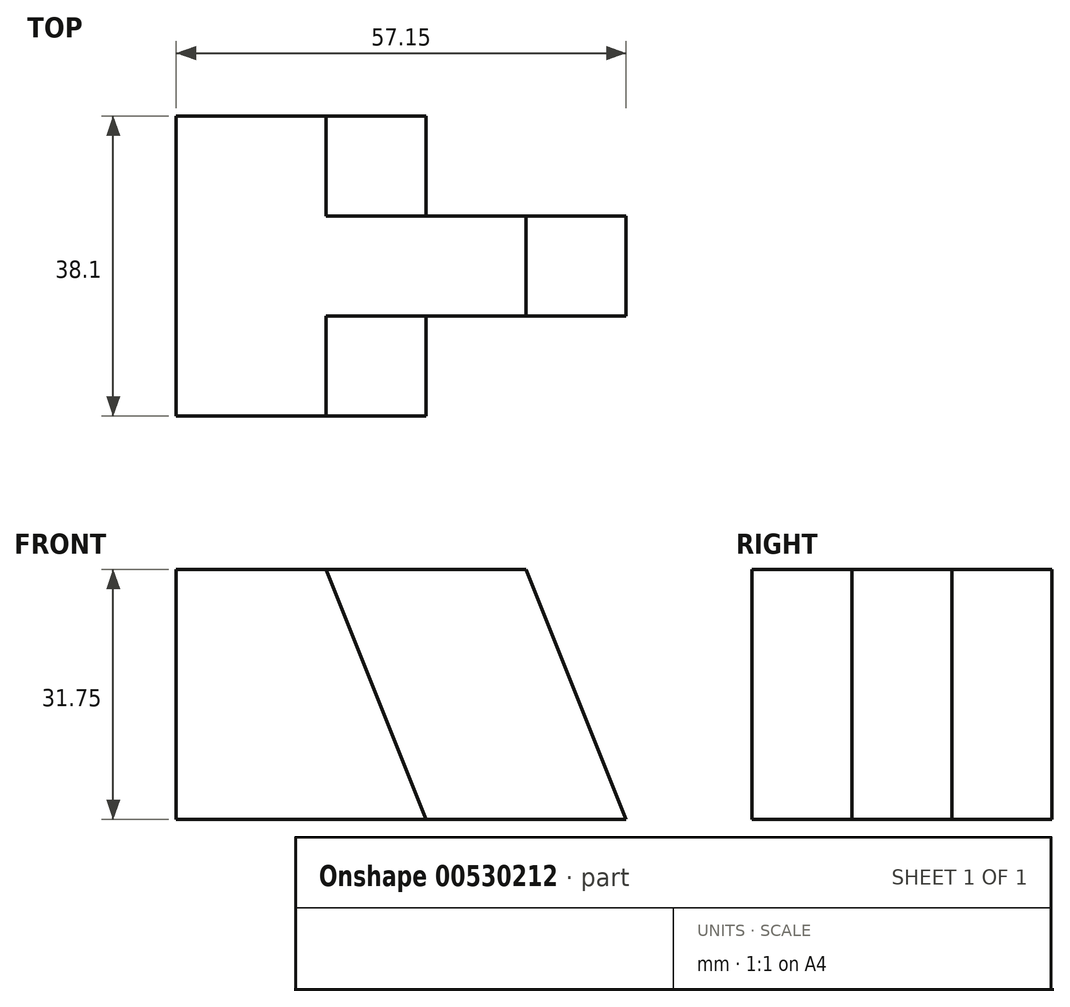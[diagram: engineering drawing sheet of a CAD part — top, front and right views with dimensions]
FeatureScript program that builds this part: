
annotation { "Feature Type Name" : "Feature", "Feature Type Description" : "" }
export const myFeature = defineFeature(function(context is Context, id is Id, definition is map)
    precondition{}
    {
        {
            var Q0;
            Q0=qCreatedBy(makeId("Top.planeOp"),FACE);
            var sketch = newSketch(context, id + "F0", { "sketchPlane" : qUnion([Q0])});
            skLineSegment(sketch, "E0", {"start": v(-47.77, 0) * mm, "end": v(-47.77, -38.1) * mm});
            skLineSegment(sketch, "E1", {"start": v(-47.77, -38.1) * mm, "end": v(-28.72, -38.1) * mm});
            skLineSegment(sketch, "E2", {"start": v(-28.72, -38.1) * mm, "end": v(-28.72, 0) * mm});
            skLineSegment(sketch, "E3", {"start": v(-28.72, 0) * mm, "end": v(-47.77, 0) * mm});
            skSolve(sketch);
        }
        {
            var Q0;
            Q0=makeQuery(id+"F0.imprint","IMPRINT",FACE,{"disambiguationData":[TD([[makeQuery(id+"F0.imprint","IMPRINT",EDGE,{"derivedFrom":sQuery(id+"F0.wireOp",EDGE,"E0")}),1.0]])]});
            extrude(context, id + "F1", {"entities" : qUnion([Q0]), "depth" : 31.75 * mm, "offsetDistance" : 25.4 * mm});
        }
        {
            var Q0;
            Q0=makeQuery(id+"F1.opExtrude","SWEPT_FACE",FACE,{"disambiguationData":[OSD([sQuery(id+"F0.wireOp",EDGE,"E2")])]});
            var sketch = newSketch(context, id + "F2", { "sketchPlane" : qUnion([Q0])});
            skLineSegment(sketch, "E4", {"start": v(-38.1, 31.75) * mm, "end": v(-25.4, 31.75) * mm});
            skLineSegment(sketch, "E5", {"start": v(-25.4, 31.75) * mm, "end": v(-25.4, 0) * mm});
            skLineSegment(sketch, "E6", {"start": v(-25.4, 0) * mm, "end": v(-38.1, 0) * mm});
            skLineSegment(sketch, "E7", {"start": v(-38.1, 0) * mm, "end": v(-38.1, 31.75) * mm});
            skSolve(sketch);
        }
        {
            var Q0;
            Q0=makeQuery(id+"F2.imprint","IMPRINT",FACE,{"disambiguationData":[TD([[makeQuery(id+"F2.imprint","IMPRINT",EDGE,{"derivedFrom":sQuery(id+"F2.wireOp",EDGE,"E4")}),-1.0]])]});
            extrude(context, id + "F3", {"entities" : qUnion([Q0]), "operationType" : NewBodyOperationType.ADD, "depth" : 12.7 * mm, "offsetDistance" : 25.4 * mm});
        }
        {
            var Q0;
            Q0=makeQuery(id+"F3.boolean.opBoolean","MERGE",FACE,{"derivedFrom":[makeQuery(id+"F1.opExtrude","SWEPT_FACE",FACE,{"disambiguationData":[OSD([sQuery(id+"F0.wireOp",EDGE,"E1")])]}),makeQuery(id+"F3.opExtrude","SWEPT_FACE",FACE,{"disambiguationData":[OSD([sQuery(id+"F2.wireOp",EDGE,"E7")])]})]});
            var sketch = newSketch(context, id + "F4", { "sketchPlane" : qUnion([Q0])});
            skLineSegment(sketch, "E8", {"start": v(-16.02, 0) * mm, "end": v(-28.72, 31.75) * mm});
            skSolve(sketch);
        }
        {
            var Q0;
            {var subQ0=sQuery(id+"F4.wireOp",EDGE,"E8");Q0=makeQuery(id+"F4.imprint","IMPRINT",FACE,{"disambiguationData":[TD([[makeQuery(id+"F4.imprint","IMPRINT",EDGE,{"derivedFrom":subQ0}),-1.0]])]});}
            extrude(context, id + "F5", {"entities" : qUnion([Q0]), "operationType" : NewBodyOperationType.REMOVE, "oppositeDirection" : true, "depth" : 25.4 * mm, "offsetDistance" : 25.4 * mm});
        }
        {
            var Q0;
            Q0=makeQuery(id+"F1.opExtrude","SWEPT_FACE",FACE,{"disambiguationData":[OSD([sQuery(id+"F0.wireOp",EDGE,"E2")])]});
            var sketch = newSketch(context, id + "F6", { "sketchPlane" : qUnion([Q0])});
            skLineSegment(sketch, "E9", {"start": v(-25.4, 31.75) * mm, "end": v(-25.4, 0) * mm});
            skLineSegment(sketch, "E10", {"start": v(-25.4, 0) * mm, "end": v(-12.7, 0) * mm});
            skLineSegment(sketch, "E11", {"start": v(-12.7, 0) * mm, "end": v(-12.7, 31.75) * mm});
            skLineSegment(sketch, "E12", {"start": v(-12.7, 31.75) * mm, "end": v(-25.4, 31.75) * mm});
            skSolve(sketch);
        }
        {
            var Q0;
            Q0 = qSketchRegion(id + "F6", true);
            extrude(context, id + "F7", {"entities" : qUnion([Q0]), "operationType" : NewBodyOperationType.ADD, "depth" : 38.1 * mm, "offsetDistance" : 25.4 * mm});
        }
        {
            var Q0;
            Q0=makeQuery(id+"F7.opExtrude","SWEPT_FACE",FACE,{"disambiguationData":[OSD([sQuery(id+"F6.wireOp",EDGE,"E9")])]});
            var sketch = newSketch(context, id + "F8", { "sketchPlane" : qUnion([Q0])});
            skLineSegment(sketch, "E13", {"start": v(9.38, 0) * mm, "end": v(-3.32, 31.75) * mm});
            skSolve(sketch);
        }
        {
            var Q0;
            {var subQ0=sQuery(id+"F8.wireOp",EDGE,"E13");Q0=makeQuery(id+"F8.imprint","IMPRINT",FACE,{"disambiguationData":[TD([[makeQuery(id+"F8.imprint","IMPRINT",EDGE,{"derivedFrom":subQ0}),-1.0]])]});}
            extrude(context, id + "F9", {"entities" : qUnion([Q0]), "operationType" : NewBodyOperationType.REMOVE, "endBound" : BoundingType.THROUGH_ALL, "oppositeDirection" : true, "depth" : 25.4 * mm, "offsetDistance" : 25.4 * mm});
        }
        {
            var Q0;
            Q0=makeQuery(id+"F1.opExtrude","SWEPT_FACE",FACE,{"disambiguationData":[OSD([sQuery(id+"F0.wireOp",EDGE,"E2")])]});
            extrude(context, id + "F10", {"entities" : qUnion([Q0]), "operationType" : NewBodyOperationType.ADD, "depth" : 12.7 * mm, "offsetDistance" : 25.4 * mm});
        }
        {
            var Q0;
            {var subQ0=sQuery(id+"F0.wireOp",EDGE,"E3");Q0=makeQuery(id+"F10.boolean.opBoolean","MERGE",FACE,{"derivedFrom":[makeQuery(id+"F1.opExtrude","SWEPT_FACE",FACE,{"disambiguationData":[OSD([subQ0])]}),makeQuery(id+"F10.opExtrude","SWEPT_FACE",FACE,{"disambiguationData":[OSD([sQuery(id+"F0.wireOp",EDGE,"E2"),subQ0])]})]});}
            var sketch = newSketch(context, id + "F11", { "sketchPlane" : qUnion([Q0])});
            skLineSegment(sketch, "E14", {"start": v(16.02, 0) * mm, "end": v(28.72, 31.75) * mm});
            skSolve(sketch);
        }
        {
            var Q0;
            {var subQ0=sQuery(id+"F11.wireOp",EDGE,"E14");Q0=makeQuery(id+"F11.imprint","IMPRINT",FACE,{"disambiguationData":[TD([[makeQuery(id+"F11.imprint","IMPRINT",EDGE,{"derivedFrom":subQ0}),1.0]])]});}
            extrude(context, id + "F12", {"entities" : qUnion([Q0]), "operationType" : NewBodyOperationType.REMOVE, "oppositeDirection" : true, "depth" : 12.7 * mm, "offsetDistance" : 25.4 * mm});
        }
    });
